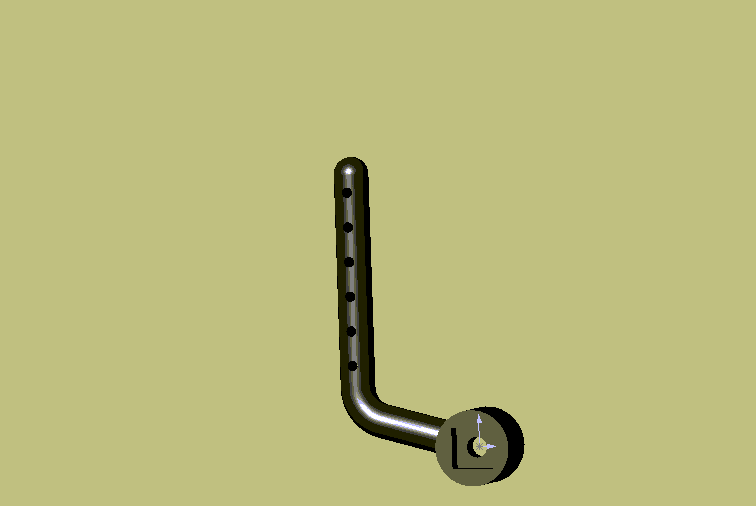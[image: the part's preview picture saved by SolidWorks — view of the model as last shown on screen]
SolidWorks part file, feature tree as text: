
SOLIDWORKS PART (.sldprt)
format: sldprt  version: not decoded by parser v0  size: 226,816 bytes
history: native  units: mm
features: sketch x6, plane x4, extrude x2, cut_extrude x2, material x1, sweep x1, fillet x1 (+8 scaffold rows collapsed)
feature tree (25):
  scaffold x8  (default folders/planes/origin — collapsed)
  material  "Matériau <non spécifié>"
  plane  "Plane1"
  plane  "Plane2"
  plane  "Plane3"
  sketch  "Esquisse1"  dims[D1=11.0mm D2=6.0mm D3=6.0mm D4=3.0mm D5=3.0mm]
  extrude  "Base-Extrusion"  Depth=8mm
  sketch  "Esquisse2"  dims[D1=11.0mm D2=6.0mm D3=6.0mm D4=3.0mm D5=3.0mm]
  extrude  "Boss.-Extru.1"  Depth=3mm
  sketch  "Esquisse3"  dims[D1=3.0mm]
  cut_extrude  "Enlèv. mat.-Extru.1"  [1 undecoded]
  sketch  "Esquisse4"  dims[c1.D3=5.0mm c1.D1=~40.853396mm c2.D1=15.0deg c2.D2=18.0mm c2.D4=42.0mm]
  plane  "Plan1"  Offset=42mm
  sketch  "Esquisse6"  dims[D1=5.0mm D2=18.0mm]
  sweep  "Boss.-Balayage1"
  fillet  "Congé1"  Radius=2.5mm
  sketch  "Esquisse7"  dims[D3=1.5mm D1=18.0mm D2=12.0mm]
  cut_extrude  "Enlèv. mat.-Extru.2"  Depth=23mm
decode coverage: 10 of 12 modeling features carry decoded parameters
note: ~ marks probable driven/reference dimensions
note: 1 parameter value undecoded
note: suppression state not decoded; provenance and decode notes live in map.json
